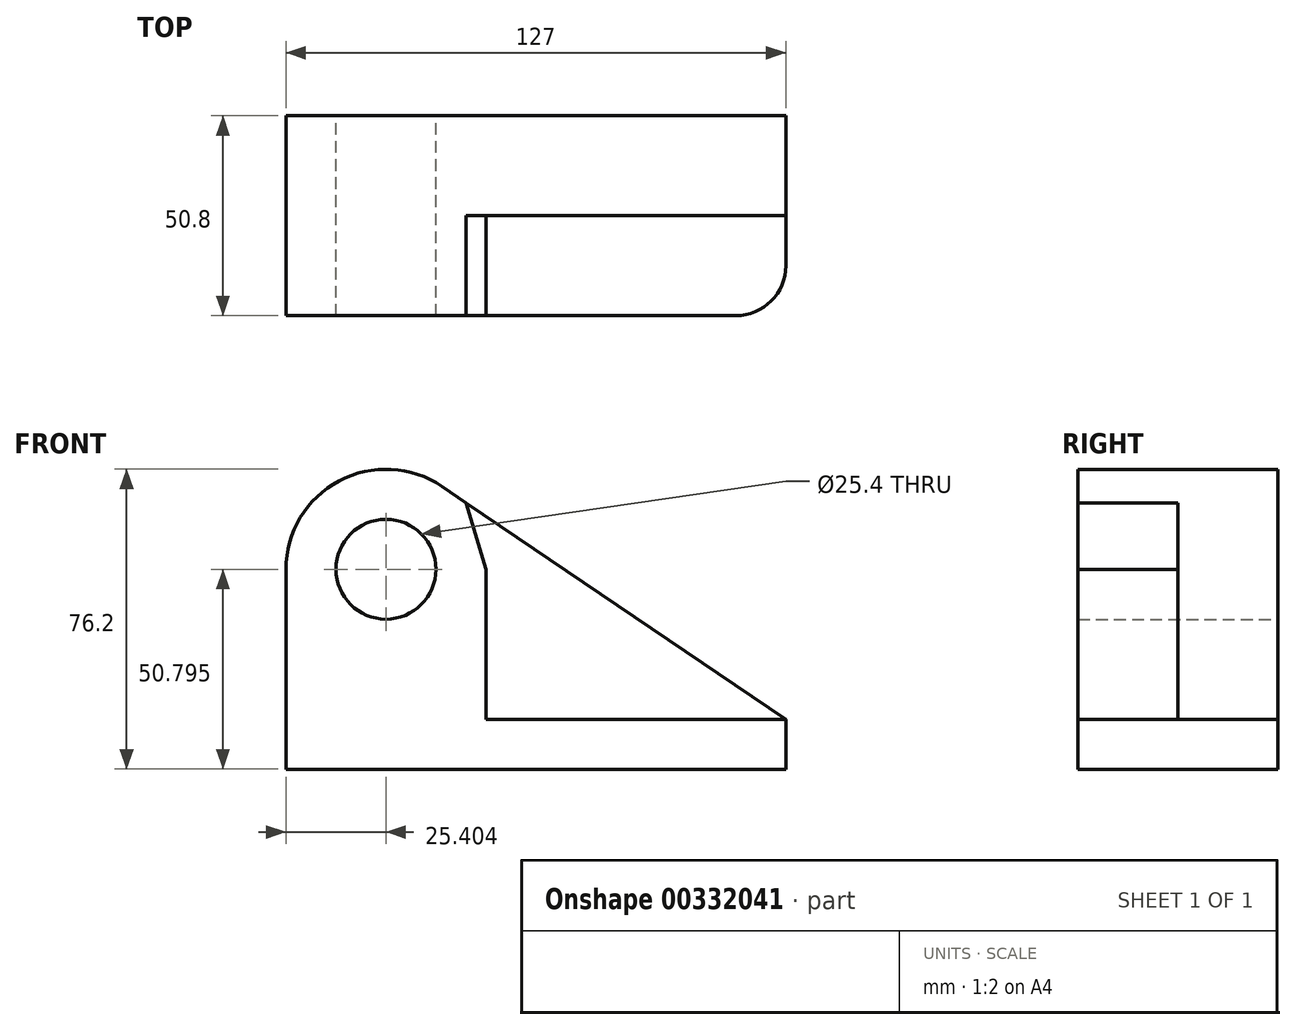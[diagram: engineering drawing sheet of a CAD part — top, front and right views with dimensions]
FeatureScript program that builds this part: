
annotation { "Feature Type Name" : "Feature", "Feature Type Description" : "" }
export const myFeature = defineFeature(function(context is Context, id is Id, definition is map)
    precondition{}
    {
        {
            var Q0;
            Q0=qCreatedBy(makeId("Front.planeOp"),FACE);
            var sketch = newSketch(context, id + "F0", { "sketchPlane" : qUnion([Q0])});
            skCircle(sketch, "E0", {"center": v(-38.72, 15.63) * mm, "radius": 12.7 * mm});
            skArc(sketch, "E1", {"start": v(-24.48, 36.66) * mm, "mid": v(-50.62, 38.06) * mm, "end": v(-64.12, 15.63) * mm});
            skLineSegment(sketch, "E2", {"start": v(-64.12, 15.63) * mm, "end": v(-64.12, -35.17) * mm});
            skLineSegment(sketch, "E3", {"start": v(-64.12, -35.17) * mm, "end": v(62.88, -35.17) * mm});
            skLineSegment(sketch, "E4", {"start": v(62.88, -35.17) * mm, "end": v(62.88, -22.47) * mm});
            skLineSegment(sketch, "E5", {"start": v(62.88, -22.47) * mm, "end": v(-24.48, 36.66) * mm});
            skSolve(sketch);
        }
        {
            var Q0;
            Q0=makeQuery(id+"F0.imprint","IMPRINT",FACE,{"disambiguationData":[TD([[makeQuery(id+"F0.imprint","IMPRINT",EDGE,{"derivedFrom":sQuery(id+"F0.wireOp",EDGE,"E0")}),-1.0]])]});
            extrude(context, id + "F1", {"entities" : qUnion([Q0]), "depth" : 25.4 * mm});
        }
        {
            var Q0;
            Q0=makeQuery(id+"F1.opExtrude","CAP_FACE",FACE,{"disambiguationData":[OSD([sQuery(id+"F0.wireOp",EDGE,"E0"),sQuery(id+"F0.wireOp",EDGE,"E1"),sQuery(id+"F0.wireOp",EDGE,"E2"),sQuery(id+"F0.wireOp",EDGE,"E3"),sQuery(id+"F0.wireOp",EDGE,"E4"),sQuery(id+"F0.wireOp",EDGE,"E5")])],"isStart":false});
            var sketch = newSketch(context, id + "F2", { "sketchPlane" : qUnion([Q0])});
            skCircle(sketch, "E6", {"center": v(-38.72, 15.63) * mm, "radius": 12.7 * mm});
            skLineSegment(sketch, "E7.bottom", {"start": v(62.88, -22.47) * mm, "end": v(-13.32, -22.47) * mm});
            skLineSegment(sketch, "E7.top", {"start": v(62.88, -35.17) * mm, "end": v(-64.12, -35.17) * mm});
            skLineSegment(sketch, "E7.left", {"start": v(62.88, -22.47) * mm, "end": v(62.88, -35.17) * mm});
            skLineSegment(sketch, "E7.right", {"start": v(-64.12, -22.47) * mm, "end": v(-64.12, -35.17) * mm});
            skLineSegment(sketch, "E8", {"start": v(-13.32, 15.63) * mm, "end": v(-13.32, -22.47) * mm});
            skLineSegment(sketch, "E9", {"start": v(-18.35, 32.51) * mm, "end": v(-13.32, 15.63) * mm});
            skSolve(sketch);
        }
        {
            var Q0;
            Q0=makeQuery(id+"F2.imprint","IMPRINT",FACE,{"disambiguationData":[TD([[makeQuery(id+"F2.imprint","IMPRINT",EDGE,{"derivedFrom":sQuery(id+"F2.wireOp",EDGE,"E6")}),-1.0]])]});
            extrude(context, id + "F3", {"entities" : qUnion([Q0]), "operationType" : NewBodyOperationType.ADD, "depth" : 25.4 * mm});
        }
        {
            var Q0;
            Q0=makeQuery(id+"F3.opExtrude","CAP_EDGE",EDGE,{"disambiguationData":[OSD([sQuery(id+"F2.wireOp",EDGE,"E7.left")])],"isStart":false});
            fillet(context, id + "F4", {"entities" : qUnion([Q0]), "radius" : 12.7 * mm, "tangentPropagation" : true, "allowEdgeOverflow" : false});
        }
    });
